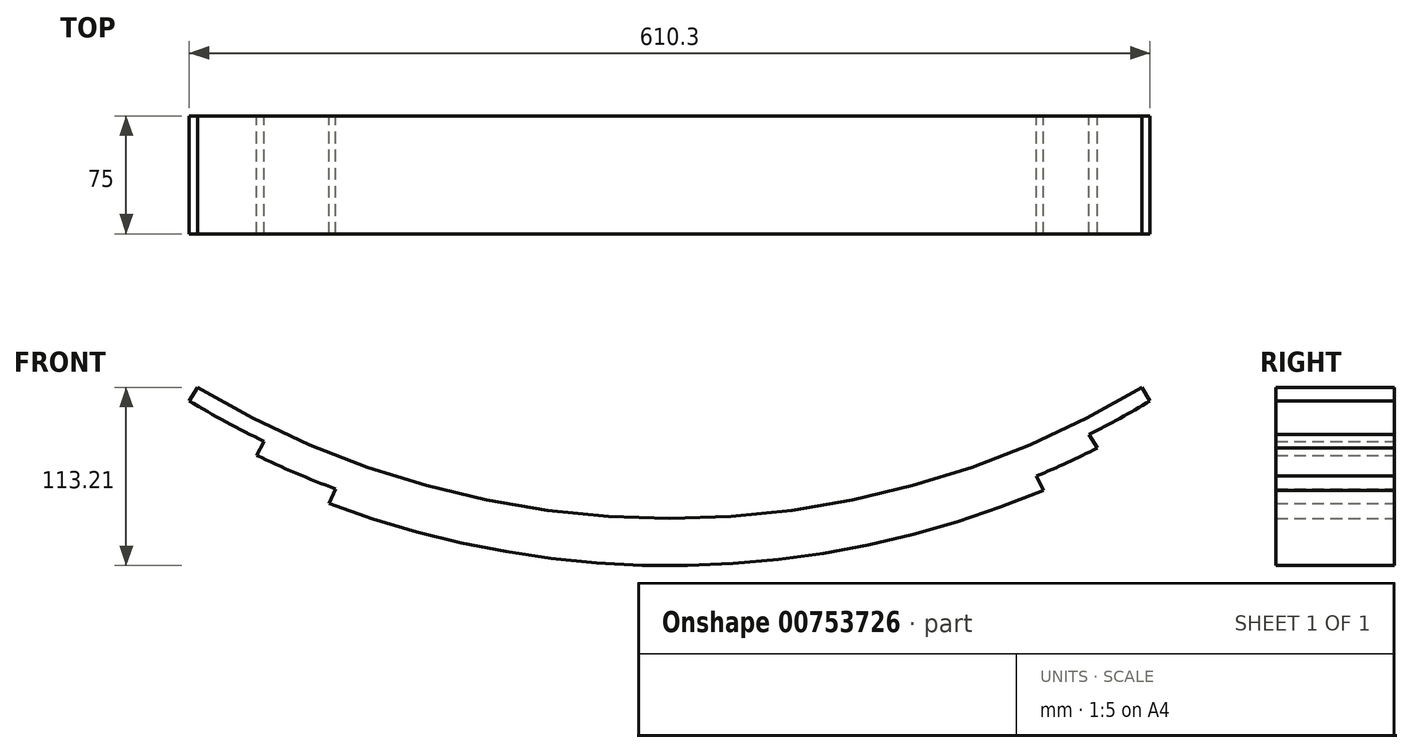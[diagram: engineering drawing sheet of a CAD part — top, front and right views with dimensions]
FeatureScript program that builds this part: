
annotation { "Feature Type Name" : "Feature", "Feature Type Description" : "" }
export const myFeature = defineFeature(function(context is Context, id is Id, definition is map)
    precondition{}
    {
        {
            var Q0;
            Q0=qCreatedBy(makeId("Front.planeOp"),FACE);
            var sketch = newSketch(context, id + "F0", { "sketchPlane" : qUnion([Q0])});
            skArc(sketch, "E0", {"start": v(-300, 0) * mm, "mid": v(0, -83.2) * mm, "end": v(300, 0) * mm});
            skArc(sketch, "E1.0", {"start": v(-305.15, -8.57) * mm, "mid": v(0, -93.2) * mm, "end": v(305.15, -8.57) * mm});
            skArc(sketch, "E2.0", {"start": v(-262.37, -43.07) * mm, "mid": v(5.17, -103.19) * mm, "end": v(271.64, -38.49) * mm});
            skArc(sketch, "E3.0", {"start": v(-216.47, -73.68) * mm, "mid": v(11.33, -113.1) * mm, "end": v(237.5, -65.28) * mm});
            skLineSegment(sketch, "E4", {"start": v(-300, 0) * mm, "end": v(-305.15, -8.57) * mm});
            skLineSegment(sketch, "E5", {"start": v(-257.72, -34.21) * mm, "end": v(-262.37, -43.07) * mm});
            skLineSegment(sketch, "E6", {"start": v(-212.33, -64.55) * mm, "end": v(-216.47, -73.68) * mm});
            skLineSegment(sketch, "E7", {"start": v(300, 0) * mm, "end": v(305.15, -8.57) * mm});
            skLineSegment(sketch, "E8", {"start": v(266.35, -29.96) * mm, "end": v(271.64, -38.49) * mm});
            skLineSegment(sketch, "E9", {"start": v(233.02, -56.32) * mm, "end": v(237.5, -65.28) * mm});
            skSolve(sketch);
        }
        {
            var Q0;
            Q0=makeQuery(id+"F0.imprint","IMPRINT",FACE,{"disambiguationData":[TD([[makeQuery(id+"F0.imprint","IMPRINT",EDGE,{"derivedFrom":sQuery(id+"F0.wireOp",EDGE,"E3.0")}),1.0]])]});
            var Q1;
            {var subQ4=sQuery(id+"F0.wireOp",EDGE,"E5");Q1=makeQuery(id+"F0.imprint","IMPRINT",FACE,{"disambiguationData":[TD([[makeQuery(id+"F0.imprint","IMPRINT",EDGE,{"derivedFrom":subQ4}),1.0]])]});}
            var Q2;
            Q2=makeQuery(id+"F0.imprint","IMPRINT",FACE,{"disambiguationData":[TD([[makeQuery(id+"F0.imprint","IMPRINT",EDGE,{"derivedFrom":sQuery(id+"F0.wireOp",EDGE,"E0")}),-1.0]])]});
            extrude(context, id + "F1", {"entities" : qUnion([Q0, Q1, Q2]), "depth" : 75 * mm, "offsetDistance" : 25 * mm});
        }
    });
